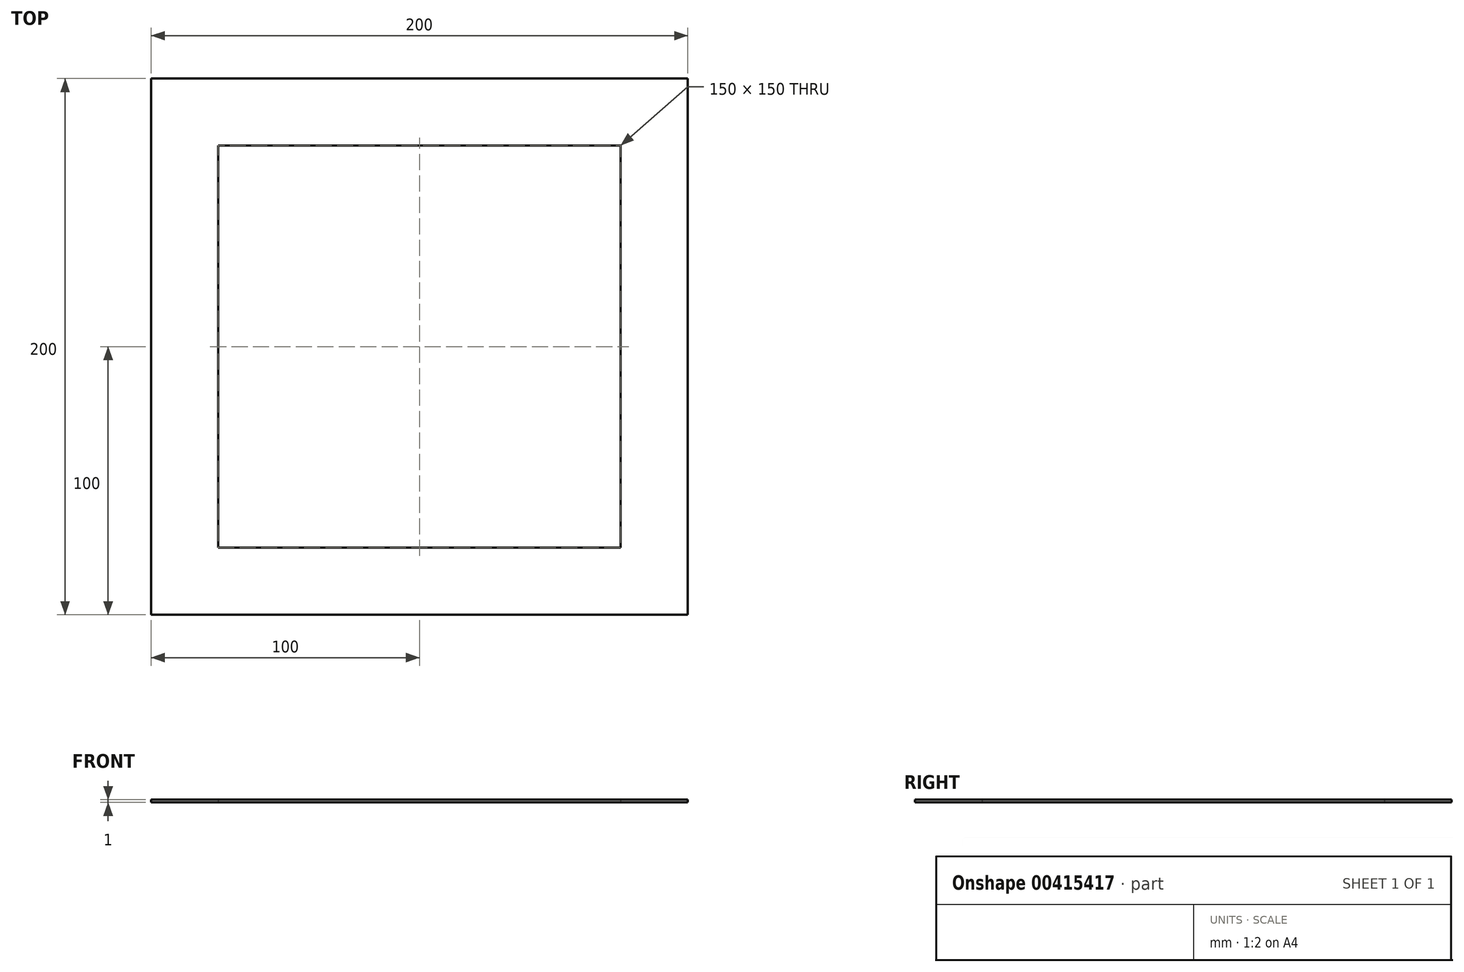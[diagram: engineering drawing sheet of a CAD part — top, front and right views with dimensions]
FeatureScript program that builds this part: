
annotation { "Feature Type Name" : "Feature", "Feature Type Description" : "" }
export const myFeature = defineFeature(function(context is Context, id is Id, definition is map)
    precondition{}
    {
        {
            var Q0;
            Q0=qCreatedBy(makeId("Top.planeOp"),FACE);
            var sketch = newSketch(context, id + "F0", { "sketchPlane" : qUnion([Q0])});
            skLineSegment(sketch, "E0.bottom", {"start": v(100, 100) * mm, "end": v(-100, 100) * mm});
            skLineSegment(sketch, "E0.top", {"start": v(100, -100) * mm, "end": v(-100, -100) * mm});
            skLineSegment(sketch, "E0.left", {"start": v(100, 100) * mm, "end": v(100, -100) * mm});
            skLineSegment(sketch, "E0.right", {"start": v(-100, 100) * mm, "end": v(-100, -100) * mm});
            skPoint(sketch, "E0.middle", {"position": v(0, 0) * mm});
            skLineSegment(sketch, "E1.bottom", {"start": v(75, 75) * mm, "end": v(-75, 75) * mm});
            skLineSegment(sketch, "E1.top", {"start": v(75, -75) * mm, "end": v(-75, -75) * mm});
            skLineSegment(sketch, "E1.left", {"start": v(75, 75) * mm, "end": v(75, -75) * mm});
            skLineSegment(sketch, "E1.right", {"start": v(-75, 75) * mm, "end": v(-75, -75) * mm});
            skSolve(sketch);
        }
        {
            var Q0;
            Q0 = qSketchRegion(id + "F0", true);
            extrude(context, id + "F1", {"entities" : qUnion([Q0]), "depth" : 1 * mm});
        }
    });
